# Revit family: Adjustable Adaptor-JCI_Sapphire_Plus-(70 bar)Novec1230
name_source: partatom
category: Specialty Equipment
revit_build: Autodesk Revit 2017 (Build: 20171027_0315(x64)
units: mm (PartAtom-declared; Revit-internal decimal feet)

## family parameters
Always vertical = Yes
Cut with Voids When Loaded = No
OmniClass Number = 23.29.33.13.11
Part Type = Normal
Room Calculation Point = No
Round Connector Dimension = Use Diameter
Shared = Yes
Work Plane-Based = Yes

## types (2) — shared parameters
Assembly Code = D4090300
Date Modified = YYYY/MM/DD
Default Elevation = 1219.2 mm  [stored 4 ft]
Description = Adjustable Height Adaptor
Equipment Abbreviation = AA
Equipment Number = XXX
Family Version = 1.0
Fire Suppression Agent = 3M™ Novec™ 1230 Fire Protection Fluid
Manufacturer = Johnson Controls, Inc.
Model Disclaimer = For More Information Contact JOHNSON CONTROLS
Product Documentation Link = http://www.sapphireplus.com
Product Page URL = http://www.sapphireplus.com
URL = http://www.sapphireplus.com

## per-type parameters (varying)
| type | BS | Model | NR | Part Number |
| 25mm | 36.25 mm | 306700003 | 16 mm | 306700003 |
| 50mm | 52.25 mm  [stored 0.171424 ft] | 306700004 | 30 mm  [stored 0.0984252 ft] | 306700004 |

note: [stored X ft] marks values corroborated as IEEE doubles in the binary element streams (Revit-internal decimal feet)

## geometry (parser evidence)
native form markers: Sweep x2
no freeform markers — native parametric forms only
